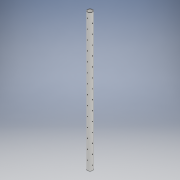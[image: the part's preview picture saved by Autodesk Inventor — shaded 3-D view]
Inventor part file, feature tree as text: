
AUTODESK INVENTOR PART (.ipt)
format: ipt  version: 2018 (Build 220112000, 112)  size: 249,856 bytes
history: native  units: mm
features: sketch x3, hole x2, extrude x1
ambient origin geometry x8: Origin, YZ Plane, XZ Plane, XY Plane, X Axis, Y Axis, Z Axis, Center Point
bodies: Solid1 (feature_tree)
feature tree (6):
  extrude  "Extrusion1"  Depth=35.052mm
  hole  "Hole2"  [1 undecoded]
  hole  "Hole3"  [1 undecoded]
  sketch  "Sketch1"  dims[d0=42.164mm d1=35.052mm]
  sketch  "Sketch3"  dims[d2=1150.0mm d3=0.0mm d19=39.20825mm]
  sketch  "Sketch4"  dims[d20=140.0mm d22=79.3mm d23=10.0mm d25=10.0mm d27=6.35mm d28=6.0mm d29=4.0mm d30=2.0mm d31=90.0deg d32=8.0mm d33=20.594885mm d34=140.0mm d36=79.3mm d37=10.0mm d39=10.0mm d41=6.35mm d42=6.0mm d43=4.0mm d44=2.0mm d45=90.0deg d46=8.0mm d47=20.594885mm]
note: 2 required parameter values undecoded (feature->parameter linkage not recoverable at this tier; creation-order binding heuristic only, values carry confidence <= 0.55)
